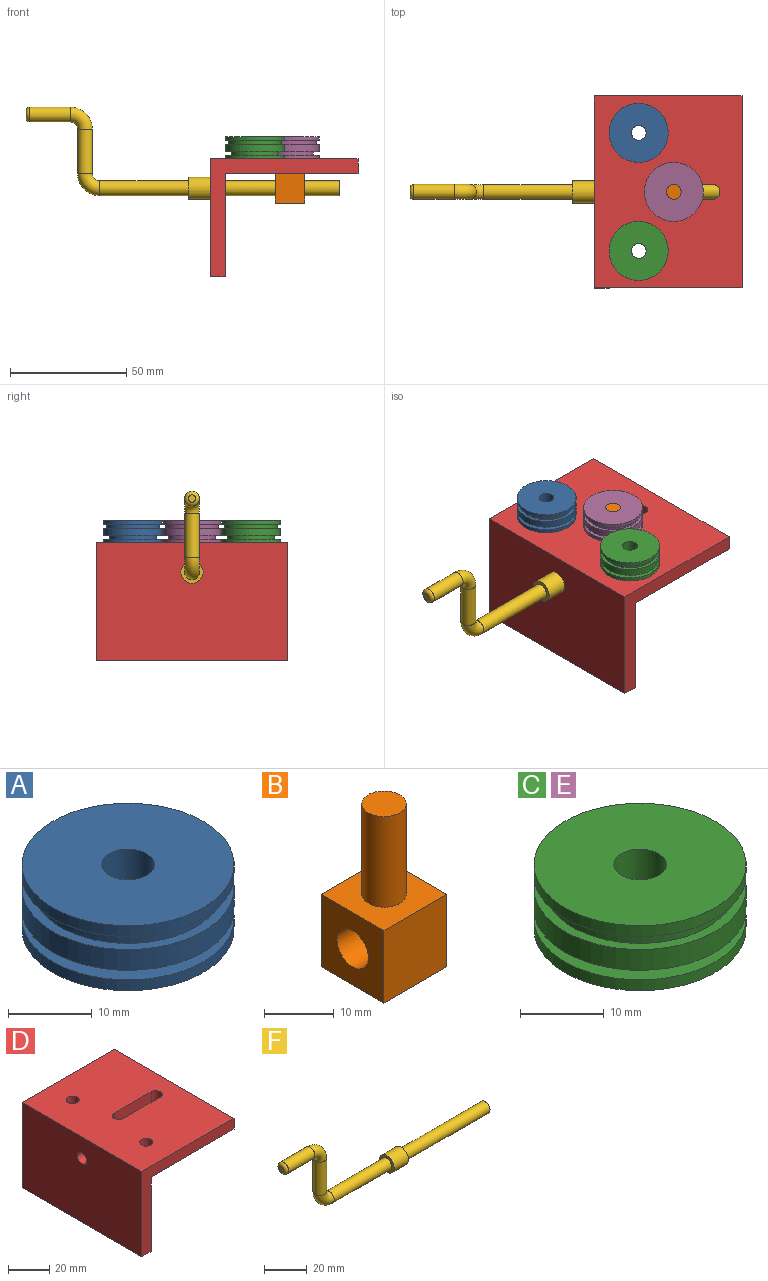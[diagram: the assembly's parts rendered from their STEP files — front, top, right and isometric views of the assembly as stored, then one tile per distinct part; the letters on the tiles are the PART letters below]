
ASSEMBLY  parts=6 mates=10
PART A: 12 faces, bbox 25.4x25.4x9.5 mm
  f0: cylinder r=12.7mm len=25.4mm, axis (0,0,1), area 126.7mm2, adj f1,f10
  f1: plane 25.4x25.4mm, normal (0,0,1), area 182.4mm2, adj f0,f2
  f2: cylinder r=10.16mm len=20.32mm, axis (0,0,1), area 89.2mm2, adj f1,f3
  f3: plane 25.4x25.4mm, normal (0,0,-1), area 182.4mm2, adj f2,f4
  f4: cylinder r=12.7mm len=25.4mm, axis (0,0,1), area 243.2mm2, adj f3,f5
  f5: plane 25.4x25.4mm, normal (0,0,1), area 96.3mm2, adj f4,f6
  f6: cylinder r=11.43mm len=22.86mm, axis (0,0,1), area 136.8mm2, adj f5,f7
  f7: plane 25.4x25.4mm, normal (0,0,-1), area 96.3mm2, adj f6,f8
  f8: cylinder r=12.7mm len=25.4mm, axis (0,0,1), area 126.7mm2, adj f7,f9
  f9: plane 25.4x25.4mm, normal (0,0,1), area 475mm2, adj f8,f11
  f10: plane 25.4x25.4mm, normal (0,0,-1), area 475mm2, adj f0,f11
  f11: cylinder r=3.17mm len=9.53mm, axis (0,0,1), area 190mm2, adj f9,f10
PART B: 9 faces, bbox 12.7x12.7x28.6 mm
  f0: plane 12.7x12.7mm, normal (1,0,0), area 129.6mm2, adj f1,f3,f4,f5,f8
  f1: plane 12.7x12.7mm, normal (0,0,1), area 129.6mm2, adj f0,f2,f4,f5,f7
  f2: plane 12.7x12.7mm, normal (-1,0,0), area 129.6mm2, adj f1,f3,f4,f5,f8
  f3: plane 12.7x12.7mm, normal (0,0,-1), area 161.3mm2, adj f0,f2,f4,f5
  f4: plane 12.7x12.7mm, normal (0,-1,0), area 161.3mm2, adj f0,f1,f2,f3
  f5: plane 12.7x12.7mm, normal (0,1,0), area 161.3mm2, adj f0,f1,f2,f3
  f6: plane 6.35x6.35mm, normal (0,0,1), area 31.7mm2, adj f7
  f7: cylinder r=3.17mm len=15.88mm, axis (0,0,-1), area 316.7mm2, adj f1,f6
  f8: cylinder r=3.17mm len=12.7mm, axis (1,0,0), area 253.4mm2, adj f0,f2
PART C: 12 faces, bbox 25.4x25.4x9.5 mm
  f0: cylinder r=12.7mm len=25.4mm, axis (0,0,1), area 126.7mm2, adj f1,f10
  f1: plane 25.4x25.4mm, normal (0,0,1), area 182.4mm2, adj f0,f2
  f2: cylinder r=10.16mm len=20.32mm, axis (0,0,1), area 89.2mm2, adj f1,f3
  f3: plane 25.4x25.4mm, normal (0,0,-1), area 182.4mm2, adj f2,f4
  f4: cylinder r=12.7mm len=25.4mm, axis (0,0,1), area 243.2mm2, adj f3,f5
  f5: plane 25.4x25.4mm, normal (0,0,1), area 96.3mm2, adj f4,f6
  f6: cylinder r=11.43mm len=22.86mm, axis (0,0,1), area 136.8mm2, adj f5,f7
  f7: plane 25.4x25.4mm, normal (0,0,-1), area 96.3mm2, adj f6,f8
  f8: cylinder r=12.7mm len=25.4mm, axis (0,0,1), area 126.7mm2, adj f7,f9
  f9: plane 25.4x25.4mm, normal (0,0,1), area 475mm2, adj f8,f11
  f10: plane 25.4x25.4mm, normal (0,0,-1), area 475mm2, adj f0,f11
  f11: cylinder r=3.17mm len=9.53mm, axis (0,0,1), area 190mm2, adj f9,f10
PART D: 15 faces, bbox 63.5x82.6x50.8 mm
  f0: plane 82.55x57.15mm, normal (0,0,-1), area 4461.4mm2, adj f2,f3,f6,f7,f8,f9,f10,f11
  f1: plane 82.55x63.5mm, normal (0,0,1), area 4985.6mm2, adj f3,f4,f6,f7,f8,f9,f10,f11
  f2: plane 82.55x44.45mm, normal (1,0,0), area 3637.7mm2, adj f0,f5,f6,f7,f14
  f3: plane 82.55x6.35mm, normal (1,0,0), area 524.2mm2, adj f0,f1,f6,f7
  f4: plane 82.55x50.8mm, normal (-1,0,0), area 4161.9mm2, adj f1,f5,f6,f7,f14
  f5: plane 82.55x6.35mm, normal (0,0,-1), area 524.2mm2, adj f2,f4,f6,f7
  f6: plane 63.5x50.8mm, normal (0,-1,0), area 685.5mm2, adj f0,f1,f2,f3,f4,f5
  f7: plane 63.5x50.8mm, normal (0,1,0), area 685.5mm2, adj f0,f1,f2,f3,f4,f5
  f8: plane 25.4x6.35mm, normal (0,-1,0), area 161.3mm2, adj f0,f1,f9,f11
  f9: cylinder r=3.17mm len=6.35mm, axis (0,0,1), area 63.3mm2, adj f0,f1,f8,f10
  f10: plane 25.4x6.35mm, normal (0,1,0), area 161.3mm2, adj f0,f1,f9,f11
  f11: cylinder r=3.17mm len=6.35mm, axis (0,0,1), area 63.3mm2, adj f0,f1,f8,f10
  f12: cylinder r=3.17mm len=6.35mm, axis (0,0,1), area 126.7mm2, adj f0,f1
  f13: cylinder r=3.17mm len=6.35mm, axis (0,0,1), area 126.7mm2, adj f0,f1
  f14: cylinder r=3.17mm len=6.35mm, axis (1,0,0), area 126.7mm2, adj f2,f4
PART E: same geometry as C
PART F: 12 faces, bbox 134.9x9.5x40.5 mm
  f0: cylinder r=3.17mm len=55.56mm, axis (1,0,0), area 1108.4mm2, adj f1,f4
  f1: plane 6.35x6.35mm, normal (1,0,0), area 31.7mm2, adj f0
  f2: cylinder r=4.76mm len=9.53mm, axis (1,0,0), area 285mm2, adj f3,f4
  f3: plane 9.53x9.53mm, normal (-1,0,0), area 39.6mm2, adj f2,f5
  f4: plane 9.53x9.53mm, normal (1,0,0), area 39.6mm2, adj f0,f2
  f5: cylinder r=3.17mm len=38.1mm, axis (1,0,0), area 760.1mm2, adj f3,f7
  f6: plane 3.18x3.18mm, normal (-1,0,0), area 7.9mm2, adj f11
  f7: torus R=6.35mm, axis (0,1,0), area 199mm2, adj f5,f8
  f8: cylinder r=3.17mm len=19.05mm, axis (0,0,1), area 380mm2, adj f7,f9
  f9: torus R=6.35mm, axis (0,-1,0), area 199mm2, adj f8,f10
  f10: cylinder r=3.17mm len=17.46mm, axis (-1,0,0), area 348.4mm2, adj f9,f11
  f11: torus R=1.59mm, axis (-1,0,0), area 40.7mm2, adj f6,f10
PLACE A t=(50.14,107.2,0.99)mm
PLACE B t=(35.07,107.2,0.99)mm
PLACE C t=(50.14,107.2,0.99)mm
PLACE D t=(50.14,107.2,0.99)mm
PLACE E t=(65.23,132.6,0.99)mm
PLACE F t=(50.14,107.2,0.99)mm
MATE planar C.f0 <-> D.f1  axis (0,0,-1) through (37.44,81.8,7.34)mm
MATE cylindrical F.f5 <-> D.f14  axis (1,0,0) through (18.39,107.2,-5.36)mm
MATE cylindrical A.f0 <-> D.f13  axis (0,0,-1) through (37.44,132.6,7.34)mm
MATE planar B.f7 <-> D.f0  axis (0,0,1) through (52.53,107.2,0.99)mm
MATE planar A.f0 <-> D.f1  axis (0,0,-1) through (37.44,132.6,7.34)mm
MATE cylindrical B.f7 <-> E.f0  axis (0,0,-1) through (52.53,107.2,8.93)mm
MATE cylindrical F.f0 <-> B.f8  axis (1,0,0) through (73.95,107.2,-5.36)mm
MATE planar D.f4 <-> F.f5  axis (-1,0,0) through (18.39,107.2,7.34)mm
MATE planar E.f0 <-> D.f1  axis (0,0,-1) through (52.53,107.2,7.34)mm
MATE cylindrical C.f0 <-> D.f12  axis (0,0,-1) through (37.44,81.8,7.34)mm
